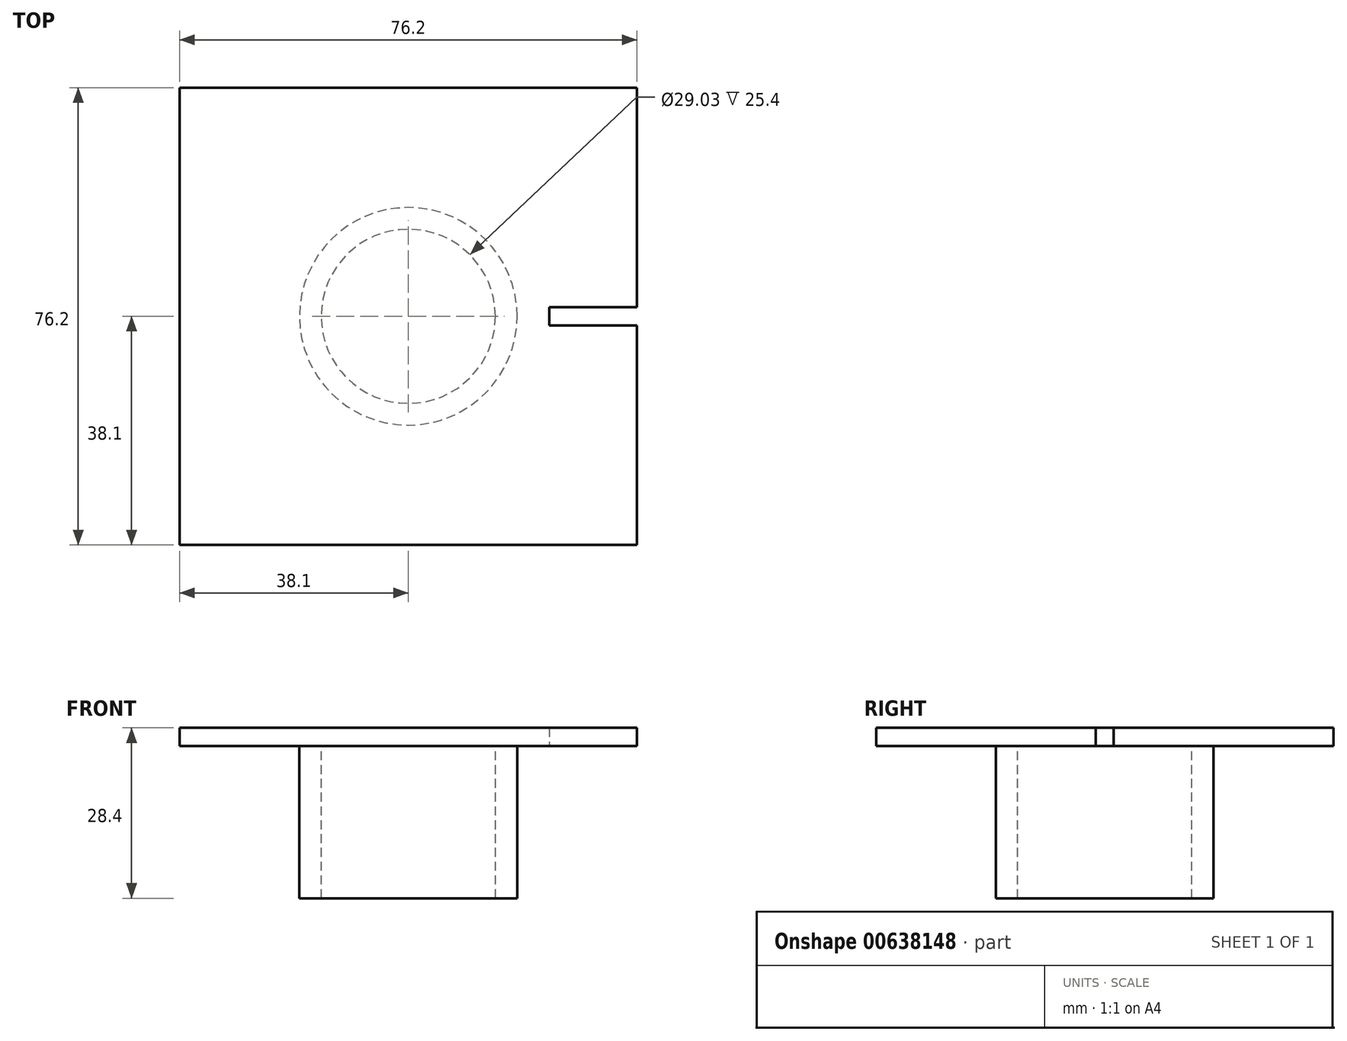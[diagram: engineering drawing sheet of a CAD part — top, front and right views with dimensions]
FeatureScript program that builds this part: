
annotation { "Feature Type Name" : "Feature", "Feature Type Description" : "" }
export const myFeature = defineFeature(function(context is Context, id is Id, definition is map)
    precondition{}
    {
        {
            assignVariable(context, id + "F0", {"name" : "x", "anyValue" : 3});
        }
        {
            var Q0;
            Q0=qCreatedBy(makeId("Top.planeOp"),FACE);
            var sketch = newSketch(context, id + "F1", { "sketchPlane" : qUnion([Q0])});
            skLineSegment(sketch, "E0.bottom", {"start": v(-38.1, 38.1) * mm, "end": v(38.1, 38.1) * mm});
            skLineSegment(sketch, "E0.top", {"start": v(-38.1, -38.1) * mm, "end": v(38.1, -38.1) * mm});
            skLineSegment(sketch, "E0.left", {"start": v(-38.1, 38.1) * mm, "end": v(-38.1, -38.1) * mm});
            skLineSegment(sketch, "E0.right", {"start": v(38.1, 38.1) * mm, "end": v(38.1, -38.1) * mm});
            skSolve(sketch);
        }
        {
            var Q0;
            Q0 = qSketchRegion(id + "F1", true);
            extrude(context, id + "F2", {"entities" : qUnion([Q0]), "depth" : (getVariable(context, 'x')) * mm, "offsetDistance" : 25.4 * mm});
        }
        {
            var Q0;
            Q0=qCreatedBy(makeId("Front.planeOp"),FACE);
            var sketch = newSketch(context, id + "F3", { "sketchPlane" : qUnion([Q0])});
            skLineSegment(sketch, "E1", {"start": v(0, 76.2) * mm, "end": v(38.45, 62.36) * mm});
            skLineSegment(sketch, "E2", {"start": v(38.45, 62.36) * mm, "end": v(38.45, 52.15) * mm});
            skLineSegment(sketch, "E3", {"start": v(38.45, 52.15) * mm, "end": v(23.52, 52.15) * mm});
            skLineSegment(sketch, "E4", {"start": v(23.52, 52.15) * mm, "end": v(23.52, 46.28) * mm});
            skLineSegment(sketch, "E5", {"start": v(23.52, 46.28) * mm, "end": v(38.68, 46.28) * mm});
            skLineSegment(sketch, "E6", {"start": v(38.68, 46.28) * mm, "end": v(38.68, 28.34) * mm});
            skLineSegment(sketch, "E7", {"start": v(38.68, 28.34) * mm, "end": v(23.52, 28.34) * mm});
            skLineSegment(sketch, "E8", {"start": v(23.52, 28.34) * mm, "end": v(38.68, 20.3) * mm});
            skLineSegment(sketch, "E9", {"start": v(38.68, 20.3) * mm, "end": v(23.52, 20.3) * mm});
            skLineSegment(sketch, "E10", {"start": v(23.52, 20.3) * mm, "end": v(23.52, 0) * mm});
            skLineSegment(sketch, "E11", {"start": v(23.52, 0) * mm, "end": v(51.2, 0) * mm});
            skLineSegment(sketch, "E12", {"start": v(51.2, 0) * mm, "end": v(51.2, 76.2) * mm});
            skLineSegment(sketch, "E13", {"start": v(51.2, 76.2) * mm, "end": v(0, 76.2) * mm});
            skSolve(sketch);
        }
        {
            var Q0;
            Q0 = qSketchRegion(id + "F3", true);
            extrude(context, id + "F4", {"entities" : qUnion([Q0]), "operationType" : NewBodyOperationType.REMOVE, "endBound" : BoundingType.SYMMETRIC, "oppositeDirection" : true, "depth" : (getVariable(context, 'x')) * mm, "offsetDistance" : 25.4 * mm});
        }
        {
            var Q0;
            Q0=qCreatedBy(makeId("Right.planeOp"),FACE);
            var sketch = newSketch(context, id + "F5", { "sketchPlane" : qUnion([Q0])});
            skLineSegment(sketch, "E14", {"start": v(0, 0) * mm, "end": v(0, 4.17) * mm});
            skSolve(sketch);
        }
        {
            var Q0;
            Q0=makeQuery(id+"F2.opExtrude","CAP_FACE",FACE,{"disambiguationData":[OSD([sQuery(id+"F1.wireOp",EDGE,"E0.bottom"),sQuery(id+"F1.wireOp",EDGE,"E0.top"),sQuery(id+"F1.wireOp",EDGE,"E0.left"),sQuery(id+"F1.wireOp",EDGE,"E0.right")])],"isStart":true});
            var sketch = newSketch(context, id + "F6", { "sketchPlane" : qUnion([Q0])});
            skCircle(sketch, "E15", {"center": v(0, 0) * mm, "radius": 18.14 * mm});
            skCircle(sketch, "E16", {"center": v(0, 0) * mm, "radius": 14.51 * mm});
            skSolve(sketch);
        }
        {
            var Q0;
            Q0 = qSketchRegion(id + "F6", true);
            extrude(context, id + "F7", {"entities" : qUnion([Q0]), "operationType" : NewBodyOperationType.ADD, "depth" : 25.4 * mm, "offsetDistance" : 25.4 * mm});
        }
    });
